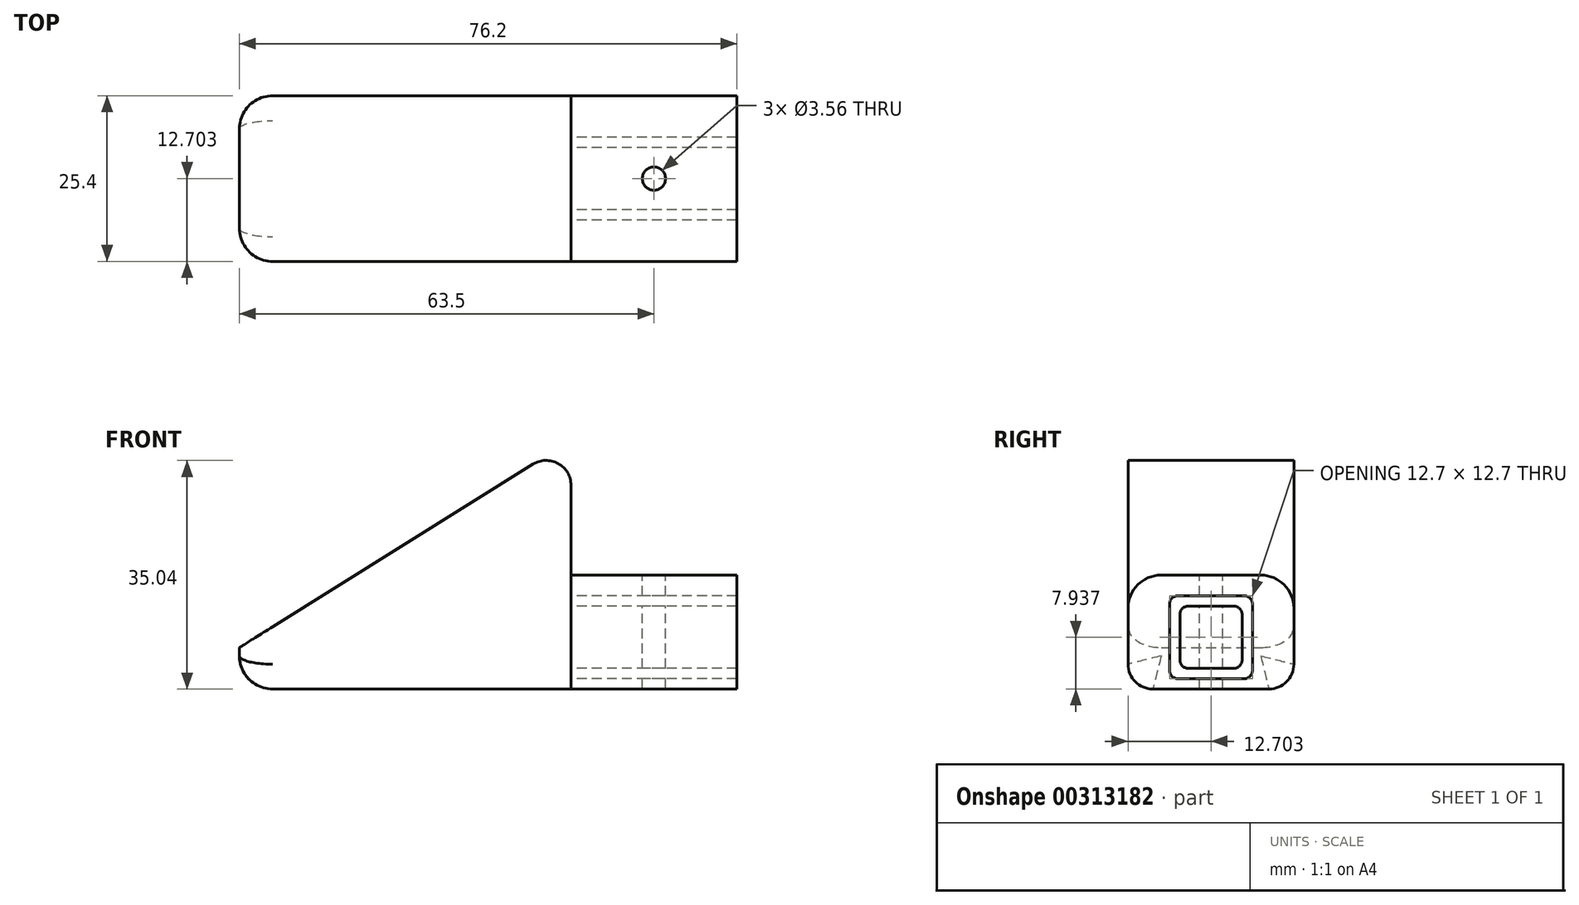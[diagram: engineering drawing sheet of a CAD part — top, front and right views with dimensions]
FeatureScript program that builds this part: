
annotation { "Feature Type Name" : "Feature", "Feature Type Description" : "" }
export const myFeature = defineFeature(function(context is Context, id is Id, definition is map)
    precondition{}
    {
        {
            var Q0;
            Q0=qCreatedBy(makeId("Right.planeOp"),FACE);
            var sketch = newSketch(context, id + "F0", { "sketchPlane" : qUnion([Q0])});
            skLineSegment(sketch, "E0.bottom", {"start": v(0, 0) * mm, "end": v(9.53, 0) * mm});
            skLineSegment(sketch, "E0.top", {"start": v(0, -9.53) * mm, "end": v(9.53, -9.53) * mm});
            skLineSegment(sketch, "E0.left", {"start": v(0, 0) * mm, "end": v(0, -9.53) * mm});
            skLineSegment(sketch, "E0.right", {"start": v(9.53, 0) * mm, "end": v(9.53, -9.53) * mm});
            skLineSegment(sketch, "E1", {"start": v(0, 0) * mm, "end": v(0, 1.59) * mm});
            skLineSegment(sketch, "E2", {"start": v(0, 0) * mm, "end": v(-1.59, 0) * mm});
            skLineSegment(sketch, "E3", {"start": v(-1.59, 0) * mm, "end": v(-1.59, 1.59) * mm});
            skLineSegment(sketch, "E4", {"start": v(-1.59, 1.59) * mm, "end": v(0, 1.59) * mm});
            skLineSegment(sketch, "E5.bottom", {"start": v(-1.59, 1.59) * mm, "end": v(11.11, 1.59) * mm});
            skLineSegment(sketch, "E5.top", {"start": v(-1.59, -11.11) * mm, "end": v(11.11, -11.11) * mm});
            skLineSegment(sketch, "E5.left", {"start": v(-1.59, 1.59) * mm, "end": v(-1.59, -11.11) * mm});
            skLineSegment(sketch, "E5.right", {"start": v(11.11, 1.59) * mm, "end": v(11.11, -11.11) * mm});
            skLineSegment(sketch, "E6", {"start": v(-1.59, -11.11) * mm, "end": v(-1.59, -12.7) * mm});
            skLineSegment(sketch, "E7", {"start": v(-1.59, -11.11) * mm, "end": v(-7.94, -11.11) * mm});
            skLineSegment(sketch, "E8", {"start": v(-7.94, -11.11) * mm, "end": v(-7.94, -12.7) * mm});
            skLineSegment(sketch, "E9", {"start": v(-7.94, -12.7) * mm, "end": v(-1.59, -12.7) * mm});
            skLineSegment(sketch, "E10", {"start": v(-1.59, 1.59) * mm, "end": v(-1.59, 4.76) * mm});
            skLineSegment(sketch, "E11", {"start": v(-1.59, 4.76) * mm, "end": v(11.11, 4.76) * mm});
            skLineSegment(sketch, "E12", {"start": v(11.11, 4.76) * mm, "end": v(11.11, 1.59) * mm});
            skLineSegment(sketch, "E13", {"start": v(11.11, 1.59) * mm, "end": v(17.46, 1.59) * mm});
            skLineSegment(sketch, "E14", {"start": v(17.46, 1.59) * mm, "end": v(17.46, 4.76) * mm});
            skLineSegment(sketch, "E15", {"start": v(17.46, 4.76) * mm, "end": v(11.11, 4.76) * mm});
            skLineSegment(sketch, "E16", {"start": v(-1.59, 4.76) * mm, "end": v(-7.94, 4.76) * mm});
            skLineSegment(sketch, "E17", {"start": v(-7.94, 4.76) * mm, "end": v(-7.94, 1.59) * mm});
            skLineSegment(sketch, "E18", {"start": v(-7.94, 1.59) * mm, "end": v(-1.59, 1.59) * mm});
            skLineSegment(sketch, "E19", {"start": v(-7.94, 1.59) * mm, "end": v(-7.94, -11.11) * mm});
            skLineSegment(sketch, "E20", {"start": v(-1.59, -12.7) * mm, "end": v(11.11, -12.7) * mm});
            skLineSegment(sketch, "E21", {"start": v(11.11, -12.7) * mm, "end": v(11.11, -11.11) * mm});
            skLineSegment(sketch, "E22", {"start": v(11.11, -12.7) * mm, "end": v(17.46, -12.7) * mm});
            skLineSegment(sketch, "E23", {"start": v(17.46, -12.7) * mm, "end": v(17.46, 1.59) * mm});
            skSolve(sketch);
        }
        {
            var Q0;
            Q0=makeQuery(id+"F0.imprint","IMPRINT",FACE,{"disambiguationData":[TD([[makeQuery(id+"F0.imprint","IMPRINT",EDGE,{"derivedFrom":sQuery(id+"F0.wireOp",EDGE,"E0.bottom")}),-1.0]])]});
            var Q1;
            {var subQ0=sQuery(id+"F0.wireOp",EDGE,"E7");Q1=makeQuery(id+"F0.imprint","IMPRINT",FACE,{"disambiguationData":[TD([[makeQuery(id+"F0.imprint","IMPRINT",EDGE,{"derivedFrom":subQ0}),-1.0]])]});}
            var Q2;
            Q2=makeQuery(id+"F0.imprint","IMPRINT",FACE,{"disambiguationData":[TD([[makeQuery(id+"F0.imprint","IMPRINT",EDGE,{"derivedFrom":sQuery(id+"F0.wireOp",EDGE,"E6")}),-1.0]])]});
            var Q3;
            Q3=makeQuery(id+"F0.imprint","IMPRINT",FACE,{"disambiguationData":[TD([[makeQuery(id+"F0.imprint","IMPRINT",EDGE,{"derivedFrom":sQuery(id+"F0.wireOp",EDGE,"E5.top")}),-1.0]])]});
            var Q4;
            Q4=makeQuery(id+"F0.imprint","IMPRINT",FACE,{"disambiguationData":[TD([[makeQuery(id+"F0.imprint","IMPRINT",EDGE,{"derivedFrom":sQuery(id+"F0.wireOp",EDGE,"E5.right")}),1.0]])]});
            var Q5;
            Q5=makeQuery(id+"F0.imprint","IMPRINT",FACE,{"disambiguationData":[TD([[makeQuery(id+"F0.imprint","IMPRINT",EDGE,{"derivedFrom":sQuery(id+"F0.wireOp",EDGE,"E10")}),1.0]])]});
            var Q6;
            {var subQ2=sQuery(id+"F0.wireOp",EDGE,"E10");Q6=makeQuery(id+"F0.imprint","IMPRINT",FACE,{"disambiguationData":[TD([[makeQuery(id+"F0.imprint","IMPRINT",EDGE,{"derivedFrom":subQ2}),-1.0]])]});}
            var Q7;
            Q7=makeQuery(id+"F0.imprint","IMPRINT",FACE,{"disambiguationData":[TD([[makeQuery(id+"F0.imprint","IMPRINT",EDGE,{"derivedFrom":sQuery(id+"F0.wireOp",EDGE,"E12")}),1.0]])]});
            extrude(context, id + "F1", {"entities" : qUnion([Q0, Q1, Q2, Q3, Q4, Q5, Q6, Q7]), "depth" : 25.4 * mm});
        }
        {
            var Q0;
            Q0=makeQuery(id+"F1.opExtrude","CAP_FACE",FACE,{"disambiguationData":[OSD([sQuery(id+"F0.wireOp",EDGE,"E5.bottom"),sQuery(id+"F0.wireOp",EDGE,"E5.top"),sQuery(id+"F0.wireOp",EDGE,"E5.left"),sQuery(id+"F0.wireOp",EDGE,"E5.right"),sQuery(id+"F0.wireOp",EDGE,"E8"),sQuery(id+"F0.wireOp",EDGE,"E9"),sQuery(id+"F0.wireOp",EDGE,"E11"),sQuery(id+"F0.wireOp",EDGE,"E14"),sQuery(id+"F0.wireOp",EDGE,"E15"),sQuery(id+"F0.wireOp",EDGE,"E16"),sQuery(id+"F0.wireOp",EDGE,"E17"),sQuery(id+"F0.wireOp",EDGE,"E19"),sQuery(id+"F0.wireOp",EDGE,"E20"),sQuery(id+"F0.wireOp",EDGE,"E22"),sQuery(id+"F0.wireOp",EDGE,"E23")])],"isStart":true});
            var sketch = newSketch(context, id + "F2", { "sketchPlane" : qUnion([Q0])});
            skLineSegment(sketch, "E24.bottom", {"start": v(-17.46, -12.7) * mm, "end": v(7.94, -12.7) * mm});
            skLineSegment(sketch, "E24.top", {"start": v(-17.46, 25.4) * mm, "end": v(7.94, 25.4) * mm});
            skLineSegment(sketch, "E24.left", {"start": v(-17.46, -12.7) * mm, "end": v(-17.46, 25.4) * mm});
            skLineSegment(sketch, "E24.right", {"start": v(7.94, -12.7) * mm, "end": v(7.94, 25.4) * mm});
            skLineSegment(sketch, "E25", {"start": v(-4.76, -12.7) * mm, "end": v(-4.76, 25.4) * mm});
            skSolve(sketch);
        }
        {
            var Q0;
            Q0 = qSketchRegion(id + "F2", true);
            extrude(context, id + "F3", {"entities" : qUnion([Q0]), "depth" : 50.8 * mm});
        }
        {
            var Q0;
            Q0=makeQuery(id+"F3.opExtrude","CAP_EDGE",EDGE,{"disambiguationData":[OSD([sQuery(id+"F2.wireOp",EDGE,"E24.top")])],"isStart":false});
            chamfer(context, id + "F4", {"entities" : qUnion([Q0]), "chamferType" : ChamferType.OFFSET_ANGLE, "width" : 50.8 * mm, "oppositeDirection" : false, "angle" : 32 * degree, "tangentPropagation" : true});
        }
        {
            var Q0;
            Q0=makeQuery(id+"F1.opExtrude","SWEPT_FACE",FACE,{"disambiguationData":[OSD([sQuery(id+"F0.wireOp",EDGE,"E11"),sQuery(id+"F0.wireOp",EDGE,"E15"),sQuery(id+"F0.wireOp",EDGE,"E16")])]});
            var sketch = newSketch(context, id + "F5", { "sketchPlane" : qUnion([Q0])});
            skLineSegment(sketch, "E26", {"start": v(25.4, 4.76) * mm, "end": v(0, 4.76) * mm});
            skLineSegment(sketch, "E27", {"start": v(0, 4.76) * mm, "end": v(12.7, -7.94) * mm});
            skLineSegment(sketch, "E28", {"start": v(12.7, -7.94) * mm, "end": v(12.7, 17.46) * mm});
            skLineSegment(sketch, "E29", {"start": v(12.7, 17.46) * mm, "end": v(25.4, 4.76) * mm});
            skLineSegment(sketch, "E30", {"start": v(0, 4.76) * mm, "end": v(12.7, 17.46) * mm});
            skLineSegment(sketch, "E31", {"start": v(12.7, -7.94) * mm, "end": v(25.4, 4.76) * mm});
            skCircle(sketch, "E32", {"center": v(12.7, 4.76) * mm, "radius": 1.78 * mm});
            skSolve(sketch);
        }
        {
            var Q0;
            {var subQ0=sQuery(id+"F5.wireOp",EDGE,"E28");var subQ1=sQuery(id+"F5.wireOp",EDGE,"E26");var subQ2=makeQuery(id+"F5.imprint","INTERSECT",VERTEX,{"derivedFrom":[subQ1,subQ0]});Q0=makeQuery(id+"F5.imprint","IMPRINT",FACE,{"disambiguationData":[TD([[makeQuery(id+"F5.imprint","IMPRINT",EDGE,{"disambiguationData":[TD([[subQ2,-1.0]])],"derivedFrom":subQ1}),-1.0]])]});}
            var Q1;
            {var subQ0=sQuery(id+"F5.wireOp",EDGE,"E28");var subQ1=sQuery(id+"F5.wireOp",EDGE,"E26");var subQ2=makeQuery(id+"F5.imprint","INTERSECT",VERTEX,{"derivedFrom":[subQ1,subQ0]});Q1=makeQuery(id+"F5.imprint","IMPRINT",FACE,{"disambiguationData":[TD([[makeQuery(id+"F5.imprint","IMPRINT",EDGE,{"disambiguationData":[TD([[subQ2,-1.0]])],"derivedFrom":subQ1}),1.0]])]});}
            var Q2;
            {var subQ0=sQuery(id+"F5.wireOp",EDGE,"E32");var subQ1=sQuery(id+"F5.wireOp",EDGE,"E26");var subQ2=makeQuery(id+"F5.imprint","INTERSECT",VERTEX,{"disambiguationData":[OD(0.0)],"derivedFrom":[subQ1,subQ0]});Q2=makeQuery(id+"F5.imprint","IMPRINT",FACE,{"disambiguationData":[TD([[makeQuery(id+"F5.imprint","IMPRINT",EDGE,{"disambiguationData":[TD([[subQ2,-1.0]])],"derivedFrom":subQ1}),1.0]])]});}
            var Q3;
            {var subQ0=sQuery(id+"F5.wireOp",EDGE,"E32");var subQ1=sQuery(id+"F5.wireOp",EDGE,"E26");var subQ2=makeQuery(id+"F5.imprint","INTERSECT",VERTEX,{"disambiguationData":[OD(0.0)],"derivedFrom":[subQ1,subQ0]});Q3=makeQuery(id+"F5.imprint","IMPRINT",FACE,{"disambiguationData":[TD([[makeQuery(id+"F5.imprint","IMPRINT",EDGE,{"disambiguationData":[TD([[subQ2,-1.0]])],"derivedFrom":subQ1}),-1.0]])]});}
            extrude(context, id + "F6", {"entities" : qUnion([Q0, Q1, Q2, Q3]), "operationType" : NewBodyOperationType.REMOVE, "endBound" : BoundingType.SYMMETRIC, "oppositeDirection" : true, "depth" : 41.45 * mm});
        }
        {
            var Q0;
            Q0=makeQuery(id+"F3.opExtrude","SWEPT_EDGE",EDGE,{"disambiguationData":[OSD([sQuery(id+"F2.wireOp",EDGE,"E24.bottom"),sQuery(id+"F2.wireOp",EDGE,"E24.right")])]});
            var Q1;
            Q1=makeQuery(id+"F3.opExtrude","SWEPT_EDGE",EDGE,{"disambiguationData":[OSD([sQuery(id+"F2.wireOp",EDGE,"E24.bottom"),sQuery(id+"F2.wireOp",EDGE,"E24.left")])]});
            var Q2;
            Q2=makeQuery(id+"F1.opExtrude","SWEPT_EDGE",EDGE,{"disambiguationData":[OSD([sQuery(id+"F0.wireOp",EDGE,"E8"),sQuery(id+"F0.wireOp",EDGE,"E9")])]});
            var Q3;
            Q3=makeQuery(id+"F1.opExtrude","SWEPT_EDGE",EDGE,{"disambiguationData":[OSD([sQuery(id+"F0.wireOp",EDGE,"E22"),sQuery(id+"F0.wireOp",EDGE,"E23")])]});
            var Q4;
            {var subQ0=sQuery(id+"F2.wireOp",EDGE,"E24.top");Q4=makeQuery(id+"F4.opChamfer","BLEND_EDGE",EDGE,{"blendedFrom":[makeQuery(id+"F3.opExtrude","CAP_EDGE",EDGE,{"disambiguationData":[OSD([subQ0])],"isStart":false}),makeQuery(id+"F3.opExtrude","CAP_FACE",FACE,{"disambiguationData":[OSD([sQuery(id+"F2.wireOp",EDGE,"E24.bottom"),subQ0,sQuery(id+"F2.wireOp",EDGE,"E24.left"),sQuery(id+"F2.wireOp",EDGE,"E24.right")])],"isStart":true})],"blendedInto":[makeQuery(id+"F3.opExtrude","CAP_FACE",FACE,{"disambiguationData":[OSD([sQuery(id+"F2.wireOp",EDGE,"E24.bottom"),subQ0,sQuery(id+"F2.wireOp",EDGE,"E24.left"),sQuery(id+"F2.wireOp",EDGE,"E24.right")])],"isStart":true})]});}
            fillet(context, id + "F7", {"entities" : qUnion([Q0, Q1, Q2, Q3, Q4]), "radius" : 3.8 * mm, "tangentPropagation" : true, "allowEdgeOverflow" : false});
        }
        {
            var Q0;
            Q0=makeQuery(id+"F3.opExtrude","CAP_EDGE",EDGE,{"disambiguationData":[OSD([sQuery(id+"F2.wireOp",EDGE,"E24.bottom")])],"isStart":false});
            fillet(context, id + "F8", {"entities" : qUnion([Q0]), "radius" : 5.08 * mm, "tangentPropagation" : true, "allowEdgeOverflow" : false});
        }
        {
            var Q0;
            Q0=makeQuery(id+"F1.opExtrude","SWEPT_EDGE",EDGE,{"disambiguationData":[OSD([sQuery(id+"F0.wireOp",EDGE,"E16"),sQuery(id+"F0.wireOp",EDGE,"E17")])]});
            var Q1;
            Q1=makeQuery(id+"F1.opExtrude","SWEPT_EDGE",EDGE,{"disambiguationData":[OSD([sQuery(id+"F0.wireOp",EDGE,"E14"),sQuery(id+"F0.wireOp",EDGE,"E15")])]});
            fillet(context, id + "F9", {"entities" : qUnion([Q0, Q1]), "radius" : 5.08 * mm, "tangentPropagation" : true, "allowEdgeOverflow" : false});
        }
        {
            var Q0;
            Q0=makeQuery(id+"F1.opExtrude","SWEPT_EDGE",EDGE,{"disambiguationData":[OSD([sQuery(id+"F0.wireOp",EDGE,"E0.bottom"),sQuery(id+"F0.wireOp",EDGE,"E0.left"),sQuery(id+"F0.wireOp",EDGE,"E1"),sQuery(id+"F0.wireOp",EDGE,"E2")])]});
            var Q1;
            Q1=makeQuery(id+"F1.opExtrude","SWEPT_EDGE",EDGE,{"disambiguationData":[OSD([sQuery(id+"F0.wireOp",EDGE,"E0.bottom"),sQuery(id+"F0.wireOp",EDGE,"E0.right")])]});
            var Q2;
            Q2=makeQuery(id+"F1.opExtrude","SWEPT_EDGE",EDGE,{"disambiguationData":[OSD([sQuery(id+"F0.wireOp",EDGE,"E0.top"),sQuery(id+"F0.wireOp",EDGE,"E0.right")])]});
            var Q3;
            Q3=makeQuery(id+"F1.opExtrude","SWEPT_EDGE",EDGE,{"disambiguationData":[OSD([sQuery(id+"F0.wireOp",EDGE,"E0.top"),sQuery(id+"F0.wireOp",EDGE,"E0.left")])]});
            fillet(context, id + "F10", {"entities" : qUnion([Q0, Q1, Q2, Q3]), "radius" : 1.27 * mm, "tangentPropagation" : true, "allowEdgeOverflow" : false});
        }
        {
            var Q0;
            Q0=makeQuery(id+"F1.opExtrude","SWEPT_EDGE",EDGE,{"disambiguationData":[OSD([sQuery(id+"F0.wireOp",EDGE,"E5.top"),sQuery(id+"F0.wireOp",EDGE,"E5.left"),sQuery(id+"F0.wireOp",EDGE,"E6"),sQuery(id+"F0.wireOp",EDGE,"E7")])]});
            var Q1;
            Q1=makeQuery(id+"F1.opExtrude","SWEPT_EDGE",EDGE,{"disambiguationData":[OSD([sQuery(id+"F0.wireOp",EDGE,"E5.bottom"),sQuery(id+"F0.wireOp",EDGE,"E5.left"),sQuery(id+"F0.wireOp",EDGE,"E10"),sQuery(id+"F0.wireOp",EDGE,"E18")])]});
            var Q2;
            Q2=makeQuery(id+"F1.opExtrude","SWEPT_EDGE",EDGE,{"disambiguationData":[OSD([sQuery(id+"F0.wireOp",EDGE,"E5.top"),sQuery(id+"F0.wireOp",EDGE,"E5.right"),sQuery(id+"F0.wireOp",EDGE,"E21")])]});
            var Q3;
            Q3=makeQuery(id+"F1.opExtrude","SWEPT_EDGE",EDGE,{"disambiguationData":[OSD([sQuery(id+"F0.wireOp",EDGE,"E5.bottom"),sQuery(id+"F0.wireOp",EDGE,"E5.right"),sQuery(id+"F0.wireOp",EDGE,"E12"),sQuery(id+"F0.wireOp",EDGE,"E13")])]});
            fillet(context, id + "F11", {"entities" : qUnion([Q0, Q1, Q2, Q3]), "radius" : 1.27 * mm, "tangentPropagation" : true, "allowEdgeOverflow" : false});
        }
    });
